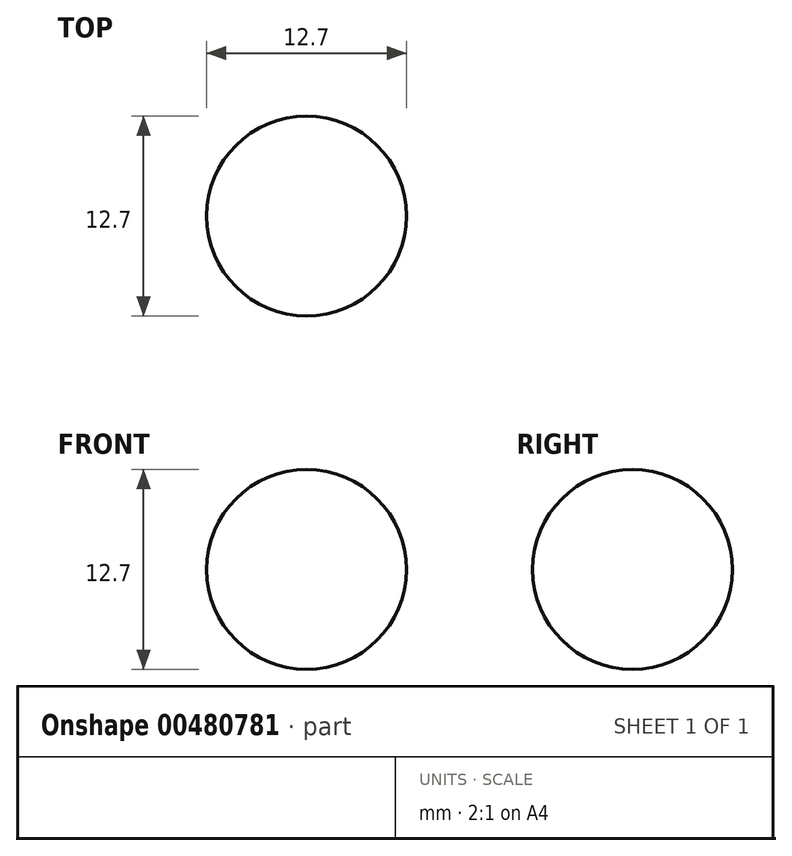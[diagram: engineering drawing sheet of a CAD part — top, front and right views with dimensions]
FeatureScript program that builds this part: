
annotation { "Feature Type Name" : "Feature", "Feature Type Description" : "" }
export const myFeature = defineFeature(function(context is Context, id is Id, definition is map)
    precondition{}
    {
        {
            var Q0;
            Q0=qCreatedBy(makeId("Front.planeOp"),FACE);
            var sketch = newSketch(context, id + "F0", { "sketchPlane" : qUnion([Q0])});
            skArc(sketch, "E0", {"start": v(0, 6.35) * mm, "mid": v(-6.35, 0) * mm, "end": v(0, -6.35) * mm});
            skLineSegment(sketch, "E1", {"start": v(0, 6.35) * mm, "end": v(0, -6.35) * mm});
            skSolve(sketch);
        }
        {
            var Q0;
            Q0 = qSketchRegion(id + "F0", true);
            var Q1;
            Q1=sQuery(id+"F0.wireOp",EDGE,"E1");
            revolve(context, id + "F1", {"entities" : qUnion([Q0]), "axis" : qUnion([Q1]), "revolveType" : RevolveType.FULL});
        }
    });
